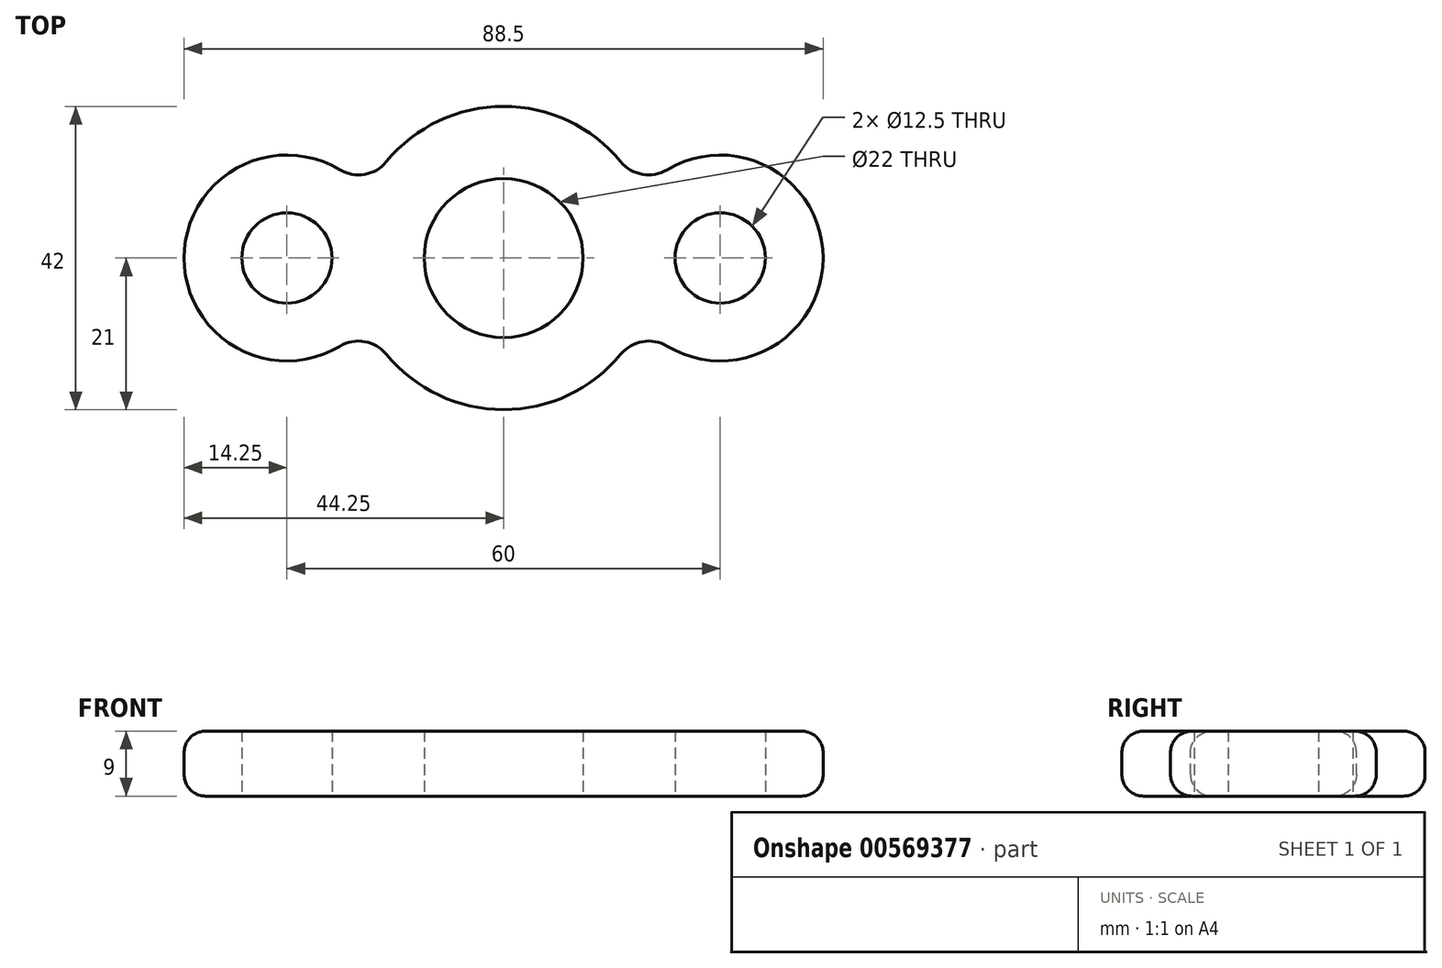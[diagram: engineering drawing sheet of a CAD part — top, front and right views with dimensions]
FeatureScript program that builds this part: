
annotation { "Feature Type Name" : "Feature", "Feature Type Description" : "" }
export const myFeature = defineFeature(function(context is Context, id is Id, definition is map)
    precondition{}
    {
        {
            var Q0;
            Q0=qCreatedBy(makeId("Top.planeOp"),FACE);
            var sketch = newSketch(context, id + "F0", { "sketchPlane" : qUnion([Q0])});
            skCircle(sketch, "E0", {"center": v(0, 0) * mm, "radius": 11 * mm});
            skCircle(sketch, "E1", {"center": v(-30, 0) * mm, "radius": 6.25 * mm});
            skCircle(sketch, "E2", {"center": v(30, 0) * mm, "radius": 6.25 * mm});
            skCircle(sketch, "E3.0", {"center": v(0, 0) * mm, "radius": 21 * mm});
            skCircle(sketch, "E4.0", {"center": v(-30, 0) * mm, "radius": 14.25 * mm});
            skCircle(sketch, "E5.0", {"center": v(30, 0) * mm, "radius": 14.25 * mm});
            skSolve(sketch);
        }
        {
            var Q0;
            Q0=makeQuery(id+"F0.imprint","IMPRINT",FACE,{"disambiguationData":[TD([[makeQuery(id+"F0.imprint","IMPRINT",EDGE,{"derivedFrom":sQuery(id+"F0.wireOp",EDGE,"E2")}),-1.0]])]});
            var Q1;
            {var subQ0=sQuery(id+"F0.wireOp",EDGE,"E4.0");var subQ1=sQuery(id+"F0.wireOp",EDGE,"E3.0");var subQ2=makeQuery(id+"F0.imprint","INTERSECT",VERTEX,{"disambiguationData":[OD(0.0)],"derivedFrom":[subQ1,subQ0]});Q1=makeQuery(id+"F0.imprint","IMPRINT",FACE,{"disambiguationData":[TD([[makeQuery(id+"F0.imprint","IMPRINT",EDGE,{"disambiguationData":[TD([[subQ2,-1.0]])],"derivedFrom":subQ1}),1.0]])]});}
            var Q2;
            {var subQ0=sQuery(id+"F0.wireOp",EDGE,"E5.0");var subQ1=sQuery(id+"F0.wireOp",EDGE,"E3.0");var subQ2=makeQuery(id+"F0.imprint","INTERSECT",VERTEX,{"disambiguationData":[OD(0.0)],"derivedFrom":[subQ1,subQ0]});Q2=makeQuery(id+"F0.imprint","IMPRINT",FACE,{"disambiguationData":[TD([[makeQuery(id+"F0.imprint","IMPRINT",EDGE,{"disambiguationData":[TD([[subQ2,1.0]])],"derivedFrom":subQ1}),1.0]])]});}
            var Q3;
            Q3=makeQuery(id+"F0.imprint","IMPRINT",FACE,{"disambiguationData":[TD([[makeQuery(id+"F0.imprint","IMPRINT",EDGE,{"derivedFrom":sQuery(id+"F0.wireOp",EDGE,"E0")}),-1.0]])]});
            var Q4;
            Q4=makeQuery(id+"F0.imprint","IMPRINT",FACE,{"disambiguationData":[TD([[makeQuery(id+"F0.imprint","IMPRINT",EDGE,{"derivedFrom":sQuery(id+"F0.wireOp",EDGE,"E1")}),-1.0]])]});
            extrude(context, id + "F1", {"entities" : qUnion([Q0, Q1, Q2, Q3, Q4]), "depth" : 9 * mm, "offsetDistance" : 25 * mm});
        }
        {
            var Q0;
            {var subQ0=sQuery(id+"F0.wireOp",EDGE,"E4.0");var subQ1=sQuery(id+"F0.wireOp",EDGE,"E3.0");Q0=makeQuery(id+"F1.opExtrude","SWEPT_EDGE",EDGE,{"disambiguationData":[OSD([subQ1,subQ0]),TDD([makeQuery(id+"F0.imprint","INTERSECT",VERTEX,{"disambiguationData":[OD(0.0)],"derivedFrom":[subQ1,subQ0]})])]});}
            var Q1;
            {var subQ0=sQuery(id+"F0.wireOp",EDGE,"E5.0");var subQ1=sQuery(id+"F0.wireOp",EDGE,"E3.0");Q1=makeQuery(id+"F1.opExtrude","SWEPT_EDGE",EDGE,{"disambiguationData":[OSD([subQ1,subQ0]),TDD([makeQuery(id+"F0.imprint","INTERSECT",VERTEX,{"disambiguationData":[OD(0.0)],"derivedFrom":[subQ1,subQ0]})])]});}
            var Q2;
            {var subQ0=sQuery(id+"F0.wireOp",EDGE,"E4.0");var subQ1=sQuery(id+"F0.wireOp",EDGE,"E3.0");Q2=makeQuery(id+"F1.opExtrude","SWEPT_EDGE",EDGE,{"disambiguationData":[OSD([subQ1,subQ0]),TDD([makeQuery(id+"F0.imprint","INTERSECT",VERTEX,{"disambiguationData":[OD(1.0)],"derivedFrom":[subQ1,subQ0]})])]});}
            var Q3;
            {var subQ0=sQuery(id+"F0.wireOp",EDGE,"E5.0");var subQ1=sQuery(id+"F0.wireOp",EDGE,"E3.0");Q3=makeQuery(id+"F1.opExtrude","SWEPT_EDGE",EDGE,{"disambiguationData":[OSD([subQ1,subQ0]),TDD([makeQuery(id+"F0.imprint","INTERSECT",VERTEX,{"disambiguationData":[OD(1.0)],"derivedFrom":[subQ1,subQ0]})])]});}
            fillet(context, id + "F2", {"entities" : qUnion([Q0, Q1, Q2, Q3]), "radius" : 5 * mm, "tangentPropagation" : true, "allowEdgeOverflow" : false});
        }
        {
            var Q0;
            Q0=makeQuery(id+"F1.opExtrude","CAP_EDGE",EDGE,{"disambiguationData":[OSD([sQuery(id+"F0.wireOp",EDGE,"E4.0")])],"isStart":false});
            var Q1;
            {var subQ0=sQuery(id+"F0.wireOp",EDGE,"E4.0");var subQ1=sQuery(id+"F0.wireOp",EDGE,"E3.0");Q1=makeQuery(id+"F2.opFillet","BLEND_EDGE",EDGE,{"blendedFrom":[makeQuery(id+"F1.opExtrude","SWEPT_EDGE",EDGE,{"disambiguationData":[OSD([subQ1,subQ0]),TDD([makeQuery(id+"F0.imprint","INTERSECT",VERTEX,{"disambiguationData":[OD(0.0)],"derivedFrom":[subQ1,subQ0]})])]}),makeQuery(id+"F1.opExtrude","CAP_FACE",FACE,{"disambiguationData":[OSD([sQuery(id+"F0.wireOp",EDGE,"E0"),sQuery(id+"F0.wireOp",EDGE,"E1"),sQuery(id+"F0.wireOp",EDGE,"E2"),subQ1,subQ0,sQuery(id+"F0.wireOp",EDGE,"E5.0")])],"isStart":false})],"blendedInto":[makeQuery(id+"F1.opExtrude","CAP_FACE",FACE,{"disambiguationData":[OSD([sQuery(id+"F0.wireOp",EDGE,"E0"),sQuery(id+"F0.wireOp",EDGE,"E1"),sQuery(id+"F0.wireOp",EDGE,"E2"),subQ1,subQ0,sQuery(id+"F0.wireOp",EDGE,"E5.0")])],"isStart":false})]});}
            var Q2;
            {var subQ0=sQuery(id+"F0.wireOp",EDGE,"E3.0");Q2=makeQuery(id+"F1.opExtrude","CAP_EDGE",EDGE,{"disambiguationData":[OSD([subQ0]),TDD([makeQuery(id+"F0.imprint","IMPRINT",EDGE,{"disambiguationData":[TD([[makeQuery(id+"F0.imprint","INTERSECT",VERTEX,{"disambiguationData":[OD(0.0)],"derivedFrom":[subQ0,sQuery(id+"F0.wireOp",EDGE,"E4.0")]}),1.0]])],"derivedFrom":subQ0})])],"isStart":false});}
            var Q3;
            {var subQ0=sQuery(id+"F0.wireOp",EDGE,"E5.0");var subQ1=sQuery(id+"F0.wireOp",EDGE,"E3.0");Q3=makeQuery(id+"F2.opFillet","BLEND_EDGE",EDGE,{"blendedFrom":[makeQuery(id+"F1.opExtrude","SWEPT_EDGE",EDGE,{"disambiguationData":[OSD([subQ1,subQ0]),TDD([makeQuery(id+"F0.imprint","INTERSECT",VERTEX,{"disambiguationData":[OD(0.0)],"derivedFrom":[subQ1,subQ0]})])]}),makeQuery(id+"F1.opExtrude","CAP_FACE",FACE,{"disambiguationData":[OSD([sQuery(id+"F0.wireOp",EDGE,"E0"),sQuery(id+"F0.wireOp",EDGE,"E1"),sQuery(id+"F0.wireOp",EDGE,"E2"),subQ1,sQuery(id+"F0.wireOp",EDGE,"E4.0"),subQ0])],"isStart":false})],"blendedInto":[makeQuery(id+"F1.opExtrude","CAP_FACE",FACE,{"disambiguationData":[OSD([sQuery(id+"F0.wireOp",EDGE,"E0"),sQuery(id+"F0.wireOp",EDGE,"E1"),sQuery(id+"F0.wireOp",EDGE,"E2"),subQ1,sQuery(id+"F0.wireOp",EDGE,"E4.0"),subQ0])],"isStart":false})]});}
            var Q4;
            Q4=makeQuery(id+"F1.opExtrude","CAP_EDGE",EDGE,{"disambiguationData":[OSD([sQuery(id+"F0.wireOp",EDGE,"E5.0")])],"isStart":false});
            var Q5;
            {var subQ0=sQuery(id+"F0.wireOp",EDGE,"E5.0");var subQ1=sQuery(id+"F0.wireOp",EDGE,"E3.0");Q5=makeQuery(id+"F2.opFillet","BLEND_EDGE",EDGE,{"blendedFrom":[makeQuery(id+"F1.opExtrude","SWEPT_EDGE",EDGE,{"disambiguationData":[OSD([subQ1,subQ0]),TDD([makeQuery(id+"F0.imprint","INTERSECT",VERTEX,{"disambiguationData":[OD(1.0)],"derivedFrom":[subQ1,subQ0]})])]}),makeQuery(id+"F1.opExtrude","CAP_FACE",FACE,{"disambiguationData":[OSD([sQuery(id+"F0.wireOp",EDGE,"E0"),sQuery(id+"F0.wireOp",EDGE,"E1"),sQuery(id+"F0.wireOp",EDGE,"E2"),subQ1,sQuery(id+"F0.wireOp",EDGE,"E4.0"),subQ0])],"isStart":false})],"blendedInto":[makeQuery(id+"F1.opExtrude","CAP_FACE",FACE,{"disambiguationData":[OSD([sQuery(id+"F0.wireOp",EDGE,"E0"),sQuery(id+"F0.wireOp",EDGE,"E1"),sQuery(id+"F0.wireOp",EDGE,"E2"),subQ1,sQuery(id+"F0.wireOp",EDGE,"E4.0"),subQ0])],"isStart":false})]});}
            var Q6;
            {var subQ0=sQuery(id+"F0.wireOp",EDGE,"E3.0");Q6=makeQuery(id+"F1.opExtrude","CAP_EDGE",EDGE,{"disambiguationData":[OSD([subQ0]),TDD([makeQuery(id+"F0.imprint","IMPRINT",EDGE,{"disambiguationData":[TD([[makeQuery(id+"F0.imprint","INTERSECT",VERTEX,{"disambiguationData":[OD(1.0)],"derivedFrom":[subQ0,sQuery(id+"F0.wireOp",EDGE,"E4.0")]}),-1.0]])],"derivedFrom":subQ0})])],"isStart":false});}
            var Q7;
            {var subQ0=sQuery(id+"F0.wireOp",EDGE,"E4.0");var subQ1=sQuery(id+"F0.wireOp",EDGE,"E3.0");Q7=makeQuery(id+"F2.opFillet","BLEND_EDGE",EDGE,{"blendedFrom":[makeQuery(id+"F1.opExtrude","SWEPT_EDGE",EDGE,{"disambiguationData":[OSD([subQ1,subQ0]),TDD([makeQuery(id+"F0.imprint","INTERSECT",VERTEX,{"disambiguationData":[OD(1.0)],"derivedFrom":[subQ1,subQ0]})])]}),makeQuery(id+"F1.opExtrude","CAP_FACE",FACE,{"disambiguationData":[OSD([sQuery(id+"F0.wireOp",EDGE,"E0"),sQuery(id+"F0.wireOp",EDGE,"E1"),sQuery(id+"F0.wireOp",EDGE,"E2"),subQ1,subQ0,sQuery(id+"F0.wireOp",EDGE,"E5.0")])],"isStart":false})],"blendedInto":[makeQuery(id+"F1.opExtrude","CAP_FACE",FACE,{"disambiguationData":[OSD([sQuery(id+"F0.wireOp",EDGE,"E0"),sQuery(id+"F0.wireOp",EDGE,"E1"),sQuery(id+"F0.wireOp",EDGE,"E2"),subQ1,subQ0,sQuery(id+"F0.wireOp",EDGE,"E5.0")])],"isStart":false})]});}
            fillet(context, id + "F3", {"entities" : qUnion([Q0, Q1, Q2, Q3, Q4, Q5, Q6, Q7]), "radius" : 3 * mm, "tangentPropagation" : true, "allowEdgeOverflow" : false});
        }
        {
            var Q0;
            {var subQ0=sQuery(id+"F0.wireOp",EDGE,"E4.0");var subQ1=sQuery(id+"F0.wireOp",EDGE,"E3.0");Q0=makeQuery(id+"F2.opFillet","BLEND_EDGE",EDGE,{"blendedFrom":[makeQuery(id+"F1.opExtrude","SWEPT_EDGE",EDGE,{"disambiguationData":[OSD([subQ1,subQ0]),TDD([makeQuery(id+"F0.imprint","INTERSECT",VERTEX,{"disambiguationData":[OD(1.0)],"derivedFrom":[subQ1,subQ0]})])]}),makeQuery(id+"F1.opExtrude","CAP_FACE",FACE,{"disambiguationData":[OSD([sQuery(id+"F0.wireOp",EDGE,"E0"),sQuery(id+"F0.wireOp",EDGE,"E1"),sQuery(id+"F0.wireOp",EDGE,"E2"),subQ1,subQ0,sQuery(id+"F0.wireOp",EDGE,"E5.0")])],"isStart":true})],"blendedInto":[makeQuery(id+"F1.opExtrude","CAP_FACE",FACE,{"disambiguationData":[OSD([sQuery(id+"F0.wireOp",EDGE,"E0"),sQuery(id+"F0.wireOp",EDGE,"E1"),sQuery(id+"F0.wireOp",EDGE,"E2"),subQ1,subQ0,sQuery(id+"F0.wireOp",EDGE,"E5.0")])],"isStart":true})]});}
            var Q1;
            Q1=makeQuery(id+"F1.opExtrude","CAP_EDGE",EDGE,{"disambiguationData":[OSD([sQuery(id+"F0.wireOp",EDGE,"E4.0")])],"isStart":true});
            var Q2;
            {var subQ0=sQuery(id+"F0.wireOp",EDGE,"E4.0");var subQ1=sQuery(id+"F0.wireOp",EDGE,"E3.0");Q2=makeQuery(id+"F2.opFillet","BLEND_EDGE",EDGE,{"blendedFrom":[makeQuery(id+"F1.opExtrude","SWEPT_EDGE",EDGE,{"disambiguationData":[OSD([subQ1,subQ0]),TDD([makeQuery(id+"F0.imprint","INTERSECT",VERTEX,{"disambiguationData":[OD(0.0)],"derivedFrom":[subQ1,subQ0]})])]}),makeQuery(id+"F1.opExtrude","CAP_FACE",FACE,{"disambiguationData":[OSD([sQuery(id+"F0.wireOp",EDGE,"E0"),sQuery(id+"F0.wireOp",EDGE,"E1"),sQuery(id+"F0.wireOp",EDGE,"E2"),subQ1,subQ0,sQuery(id+"F0.wireOp",EDGE,"E5.0")])],"isStart":true})],"blendedInto":[makeQuery(id+"F1.opExtrude","CAP_FACE",FACE,{"disambiguationData":[OSD([sQuery(id+"F0.wireOp",EDGE,"E0"),sQuery(id+"F0.wireOp",EDGE,"E1"),sQuery(id+"F0.wireOp",EDGE,"E2"),subQ1,subQ0,sQuery(id+"F0.wireOp",EDGE,"E5.0")])],"isStart":true})]});}
            var Q3;
            {var subQ0=sQuery(id+"F0.wireOp",EDGE,"E3.0");Q3=makeQuery(id+"F1.opExtrude","CAP_EDGE",EDGE,{"disambiguationData":[OSD([subQ0]),TDD([makeQuery(id+"F0.imprint","IMPRINT",EDGE,{"disambiguationData":[TD([[makeQuery(id+"F0.imprint","INTERSECT",VERTEX,{"disambiguationData":[OD(0.0)],"derivedFrom":[subQ0,sQuery(id+"F0.wireOp",EDGE,"E4.0")]}),1.0]])],"derivedFrom":subQ0})])],"isStart":true});}
            var Q4;
            {var subQ0=sQuery(id+"F0.wireOp",EDGE,"E5.0");var subQ1=sQuery(id+"F0.wireOp",EDGE,"E3.0");Q4=makeQuery(id+"F2.opFillet","BLEND_EDGE",EDGE,{"blendedFrom":[makeQuery(id+"F1.opExtrude","SWEPT_EDGE",EDGE,{"disambiguationData":[OSD([subQ1,subQ0]),TDD([makeQuery(id+"F0.imprint","INTERSECT",VERTEX,{"disambiguationData":[OD(0.0)],"derivedFrom":[subQ1,subQ0]})])]}),makeQuery(id+"F1.opExtrude","CAP_FACE",FACE,{"disambiguationData":[OSD([sQuery(id+"F0.wireOp",EDGE,"E0"),sQuery(id+"F0.wireOp",EDGE,"E1"),sQuery(id+"F0.wireOp",EDGE,"E2"),subQ1,sQuery(id+"F0.wireOp",EDGE,"E4.0"),subQ0])],"isStart":true})],"blendedInto":[makeQuery(id+"F1.opExtrude","CAP_FACE",FACE,{"disambiguationData":[OSD([sQuery(id+"F0.wireOp",EDGE,"E0"),sQuery(id+"F0.wireOp",EDGE,"E1"),sQuery(id+"F0.wireOp",EDGE,"E2"),subQ1,sQuery(id+"F0.wireOp",EDGE,"E4.0"),subQ0])],"isStart":true})]});}
            var Q5;
            Q5=makeQuery(id+"F1.opExtrude","CAP_EDGE",EDGE,{"disambiguationData":[OSD([sQuery(id+"F0.wireOp",EDGE,"E5.0")])],"isStart":true});
            var Q6;
            {var subQ0=sQuery(id+"F0.wireOp",EDGE,"E3.0");Q6=makeQuery(id+"F1.opExtrude","CAP_EDGE",EDGE,{"disambiguationData":[OSD([subQ0]),TDD([makeQuery(id+"F0.imprint","IMPRINT",EDGE,{"disambiguationData":[TD([[makeQuery(id+"F0.imprint","INTERSECT",VERTEX,{"disambiguationData":[OD(1.0)],"derivedFrom":[subQ0,sQuery(id+"F0.wireOp",EDGE,"E4.0")]}),-1.0]])],"derivedFrom":subQ0})])],"isStart":true});}
            var Q7;
            {var subQ0=sQuery(id+"F0.wireOp",EDGE,"E5.0");var subQ1=sQuery(id+"F0.wireOp",EDGE,"E3.0");Q7=makeQuery(id+"F2.opFillet","BLEND_EDGE",EDGE,{"blendedFrom":[makeQuery(id+"F1.opExtrude","SWEPT_EDGE",EDGE,{"disambiguationData":[OSD([subQ1,subQ0]),TDD([makeQuery(id+"F0.imprint","INTERSECT",VERTEX,{"disambiguationData":[OD(1.0)],"derivedFrom":[subQ1,subQ0]})])]}),makeQuery(id+"F1.opExtrude","CAP_FACE",FACE,{"disambiguationData":[OSD([sQuery(id+"F0.wireOp",EDGE,"E0"),sQuery(id+"F0.wireOp",EDGE,"E1"),sQuery(id+"F0.wireOp",EDGE,"E2"),subQ1,sQuery(id+"F0.wireOp",EDGE,"E4.0"),subQ0])],"isStart":true})],"blendedInto":[makeQuery(id+"F1.opExtrude","CAP_FACE",FACE,{"disambiguationData":[OSD([sQuery(id+"F0.wireOp",EDGE,"E0"),sQuery(id+"F0.wireOp",EDGE,"E1"),sQuery(id+"F0.wireOp",EDGE,"E2"),subQ1,sQuery(id+"F0.wireOp",EDGE,"E4.0"),subQ0])],"isStart":true})]});}
            fillet(context, id + "F4", {"entities" : qUnion([Q0, Q1, Q2, Q3, Q4, Q5, Q6, Q7]), "radius" : 3 * mm, "tangentPropagation" : true, "allowEdgeOverflow" : false});
        }
    });
